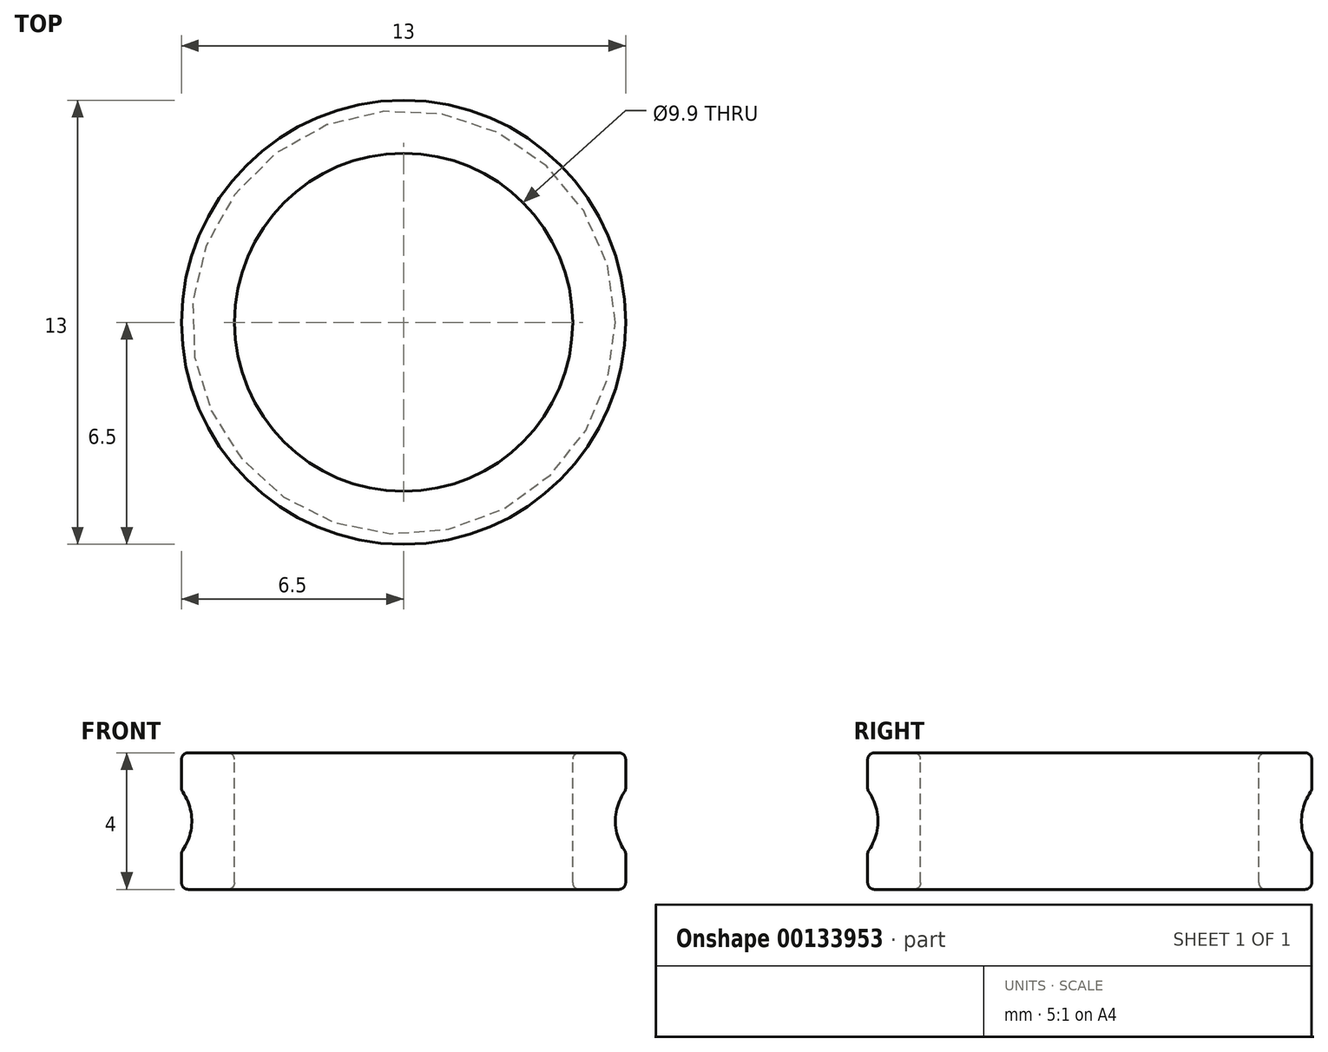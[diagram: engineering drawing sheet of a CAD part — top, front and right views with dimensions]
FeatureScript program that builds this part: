
annotation { "Feature Type Name" : "Feature", "Feature Type Description" : "" }
export const myFeature = defineFeature(function(context is Context, id is Id, definition is map)
    precondition{}
    {
        {
            var Q0;
            Q0=qCreatedBy(makeId("Front.planeOp"),FACE);
            var sketch = newSketch(context, id + "F0", { "sketchPlane" : qUnion([Q0])});
            skLineSegment(sketch, "E0", {"start": v(0, 61.7) * mm, "end": v(0, -68.95) * mm, "construction": true});
            skLineSegment(sketch, "E1", {"start": v(4.95, 0.2) * mm, "end": v(4.95, 3.8) * mm});
            skLineSegment(sketch, "E2", {"start": v(5.15, 4) * mm, "end": v(6.3, 4) * mm});
            skLineSegment(sketch, "E3", {"start": v(6.5, 3.8) * mm, "end": v(6.5, 2.96) * mm});
            skLineSegment(sketch, "E4", {"start": v(6.3, 0) * mm, "end": v(5.15, 0) * mm});
            skArc(sketch, "E5", {"start": v(6.46, 2.85) * mm, "mid": v(6.2, 2) * mm, "end": v(6.46, 1.15) * mm});
            skLineSegment(sketch, "E6.trimOffspring", {"start": v(6.5, 1.04) * mm, "end": v(6.5, 0.2) * mm});
            skPoint(sketch, "E7.visualSharp", {"position": v(6.5, 4) * mm});
            skArc(sketch, "E7.filletArc", {"start": v(6.5, 3.8) * mm, "mid": v(6.44, 3.94) * mm, "end": v(6.3, 4) * mm});
            skPoint(sketch, "E8.visualSharp", {"position": v(6.5, 0) * mm});
            skArc(sketch, "E8.filletArc", {"start": v(6.3, 0) * mm, "mid": v(6.44, 0.06) * mm, "end": v(6.5, 0.2) * mm});
            skPoint(sketch, "E9.visualSharp", {"position": v(4.95, 0) * mm});
            skArc(sketch, "E9.filletArc", {"start": v(4.95, 0.2) * mm, "mid": v(5, 0.06) * mm, "end": v(5.15, 0) * mm});
            skPoint(sketch, "E10.visualSharp", {"position": v(4.95, 4) * mm});
            skArc(sketch, "E10.filletArc", {"start": v(5.15, 4) * mm, "mid": v(5, 3.94) * mm, "end": v(4.95, 3.8) * mm});
            skPoint(sketch, "E11.visualSharp", {"position": v(6.5, 2.9) * mm});
            skArc(sketch, "E11.filletArc", {"start": v(6.46, 2.85) * mm, "mid": v(6.5, 2.9) * mm, "end": v(6.5, 2.96) * mm});
            skPoint(sketch, "E12.visualSharp", {"position": v(6.5, 1.1) * mm});
            skArc(sketch, "E12.filletArc", {"start": v(6.5, 1.04) * mm, "mid": v(6.5, 1.1) * mm, "end": v(6.46, 1.15) * mm});
            skSolve(sketch);
        }
        {
            var Q0;
            Q0=makeQuery(id+"F0.imprint","IMPRINT",FACE,{"disambiguationData":[TD([[makeQuery(id+"F0.imprint","IMPRINT",EDGE,{"derivedFrom":sQuery(id+"F0.wireOp",EDGE,"E1")}),-1.0]])]});
            var Q1;
            Q1=sQuery(id+"F0.wireOp",EDGE,"E0");
            revolve(context, id + "F1", {"surfaceOperationType" : NewSurfaceOperationType.NEW, "entities" : qUnion([Q0]), "axis" : qUnion([Q1]), "revolveType" : RevolveType.FULL});
        }
    });
